# Revit family: Louver Classic 1 Panel
name_source: partatom
category: Generic Models
revit_build: Autodesk Revit 2017 (Build: 20160225_1515(x64)
units: mm (PartAtom-declared; Revit-internal decimal feet)

## family parameters
Always vertical = No
Can host rebar = No
Cut with Voids When Loaded = No
Part Type = Normal
Room Calculation Point = No
Round Connector Dimension = Use Diameter
Shared = No
Work Plane-Based = Yes

## types (1)
- Louver Classic 1 Panel
    Bottom Rail = 0' - 4"
    Default Elevation = 4' - 0"
    Finish Color = Default
    Louver Length = 1' - 2"
    Louver Section 1 = 5' - 3"
    Manufacturer = New Horizon Shutters
    Model = Louver Classic
    Shutter Height = 6' - 0"
    Shutter Width = 1' - 6"
    ShutterThickness = 0' - 1 1/4"
    Tilt Rod = Yes
    Top Rail = 0' - 3 1/4"
    Type Comments = **** All shutter dimensions and configurations to be approved by NHSI ****
    URL = www.newhorizonshutters.com

## geometry (parser evidence)
native form markers: Sweep x14
no freeform markers — native parametric forms only
